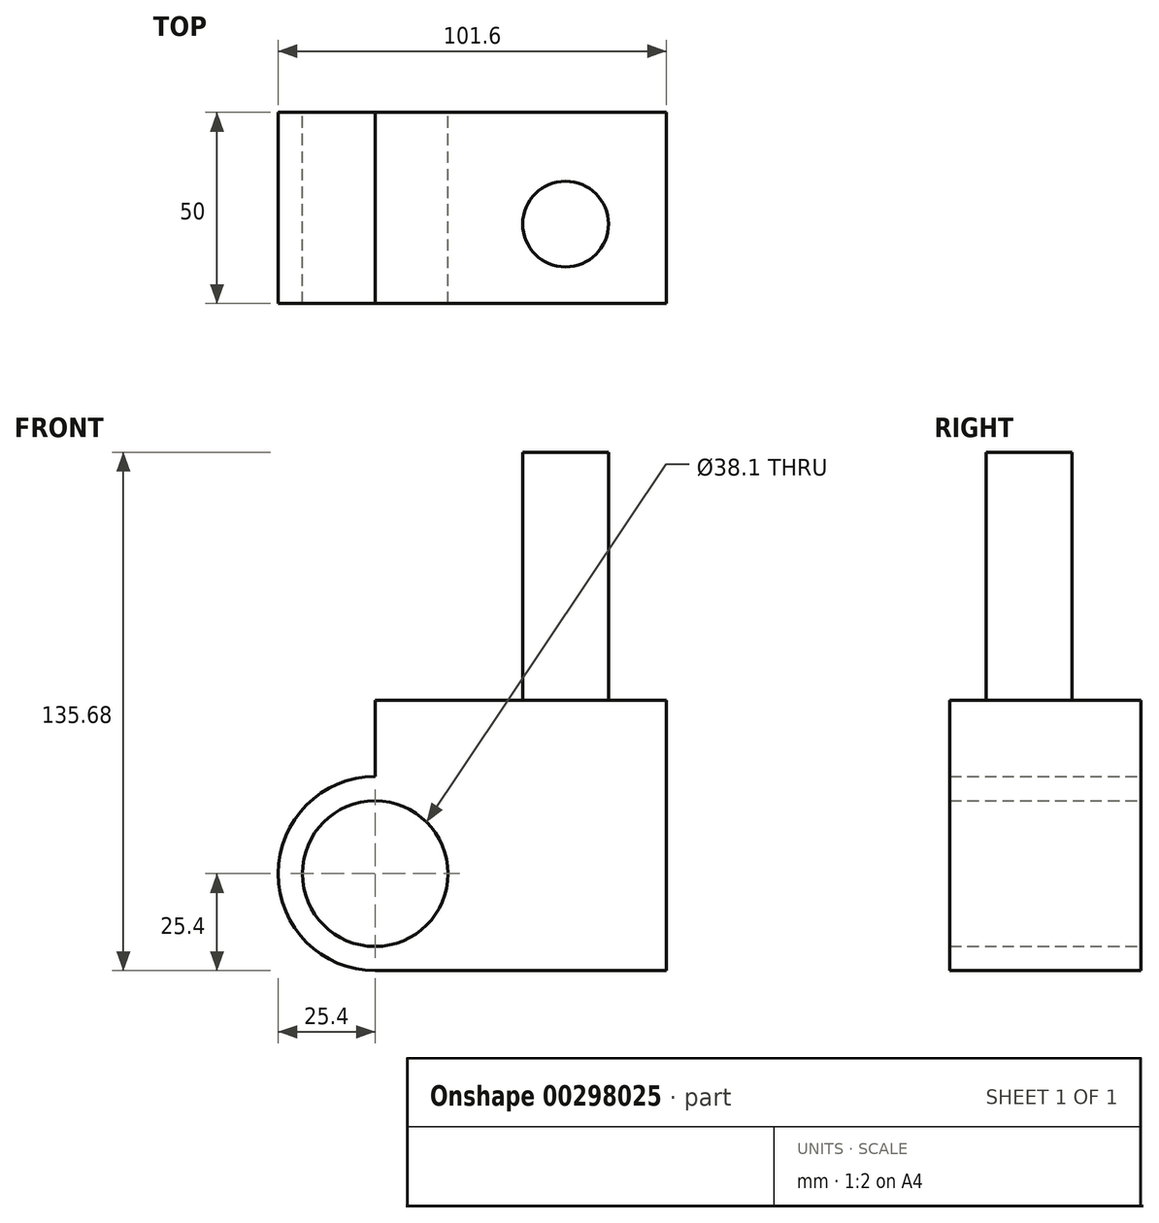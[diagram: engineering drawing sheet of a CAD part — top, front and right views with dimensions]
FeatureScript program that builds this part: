
annotation { "Feature Type Name" : "Feature", "Feature Type Description" : "" }
export const myFeature = defineFeature(function(context is Context, id is Id, definition is map)
    precondition{}
    {
        {
            var Q0;
            Q0=qCreatedBy(makeId("Front.planeOp"),FACE);
            var sketch = newSketch(context, id + "F0", { "sketchPlane" : qUnion([Q0])});
            skLineSegment(sketch, "E0.bottom", {"start": v(38.1, -25.4) * mm, "end": v(-38.1, -25.4) * mm});
            skLineSegment(sketch, "E0.top", {"start": v(38.1, 25.4) * mm, "end": v(-38.1, 25.4) * mm});
            skLineSegment(sketch, "E0.left", {"start": v(38.1, -25.4) * mm, "end": v(38.1, 25.4) * mm});
            skLineSegment(sketch, "E0.right", {"start": v(-38.1, -25.4) * mm, "end": v(-38.1, 25.4) * mm});
            skPoint(sketch, "E0.middle", {"position": v(0, 0) * mm});
            skCircle(sketch, "E1", {"center": v(-38.1, 0) * mm, "radius": 25.4 * mm});
            skCircle(sketch, "E2", {"center": v(-38.1, 0) * mm, "radius": 19.05 * mm});
            skSolve(sketch);
        }
        {
            var Q0;
            Q0 = qSketchRegion(id + "F0", true);
            extrude(context, id + "F1", {"entities" : qUnion([Q0]), "depth" : 50 * mm});
        }
        {
            var Q0;
            Q0=makeQuery(id+"F1.opExtrude","SWEPT_FACE",FACE,{"disambiguationData":[OSD([sQuery(id+"F0.wireOp",EDGE,"E0.top")])]});
            extrude(context, id + "F2", {"entities" : qUnion([Q0]), "operationType" : NewBodyOperationType.ADD, "depth" : 20 * mm});
        }
        {
            var Q0;
            Q0=makeQuery(id+"F2.opExtrude","CAP_FACE",FACE,{"disambiguationData":[OSD([sQuery(id+"F0.wireOp",EDGE,"E0.top")])],"isStart":false});
            var sketch = newSketch(context, id + "F3", { "sketchPlane" : qUnion([Q0])});
            skCircle(sketch, "E3", {"center": v(11.73, -29.23) * mm, "radius": 11.22 * mm});
            skSolve(sketch);
        }
        {
            var Q0;
            Q0 = qSketchRegion(id + "F3", true);
            extrude(context, id + "F4", {"entities" : qUnion([Q0]), "operationType" : NewBodyOperationType.ADD, "depth" : 64.88 * mm});
        }
    });
